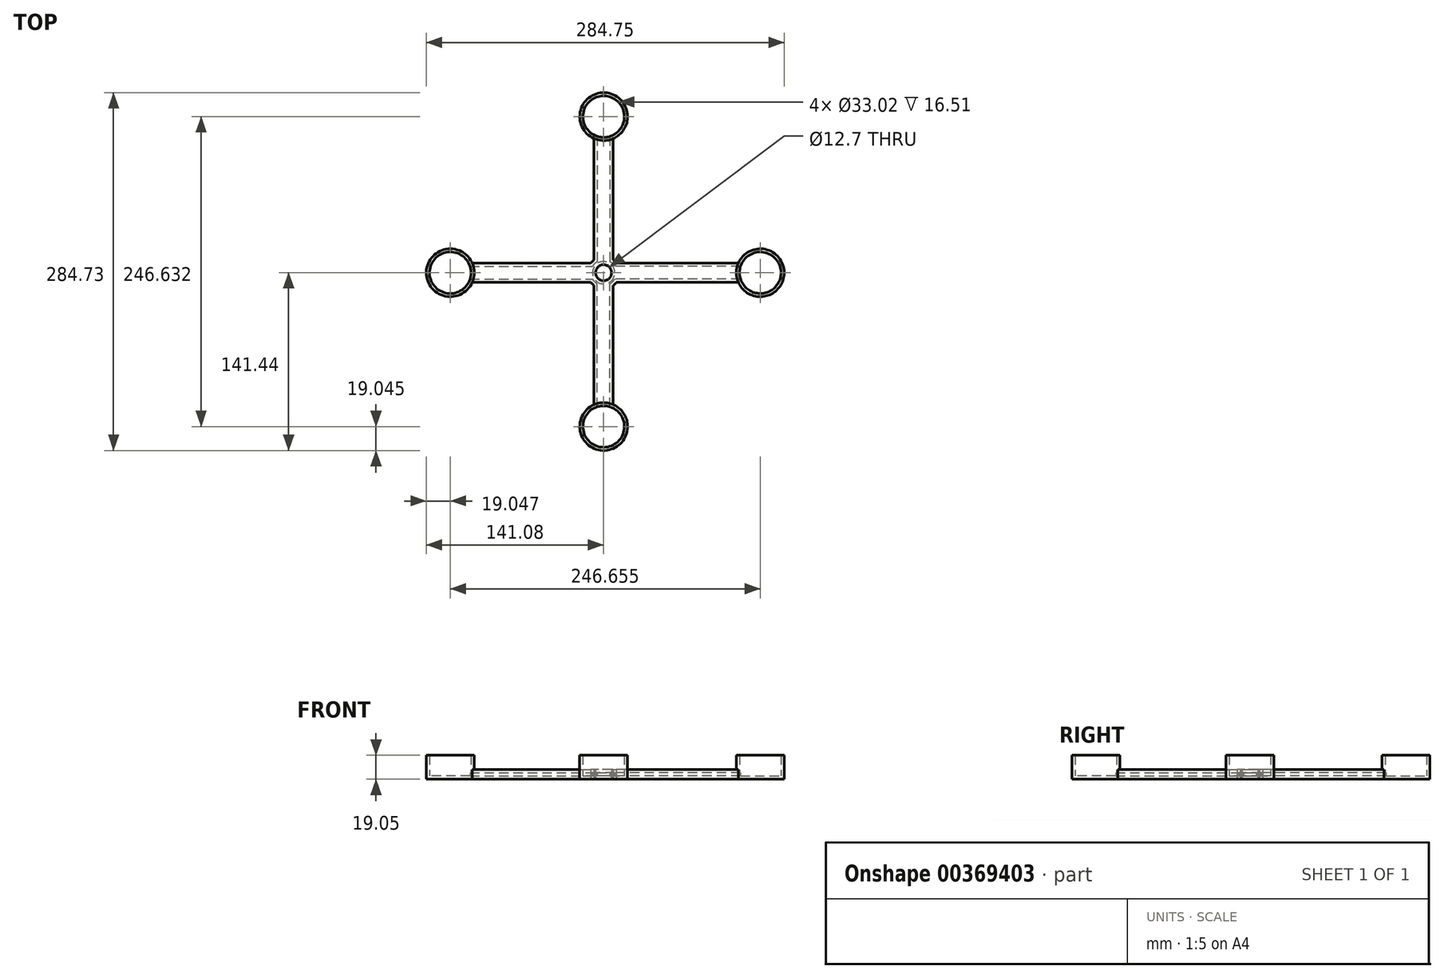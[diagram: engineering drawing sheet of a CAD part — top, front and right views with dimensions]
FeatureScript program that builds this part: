
annotation { "Feature Type Name" : "Feature", "Feature Type Description" : "" }
export const myFeature = defineFeature(function(context is Context, id is Id, definition is map)
    precondition{}
    {
        {
            var Q0;
            Q0=qCreatedBy(makeId("Top.planeOp"),FACE);
            var sketch = newSketch(context, id + "F0", { "sketchPlane" : qUnion([Q0])});
            skCircle(sketch, "E0", {"center": v(0, 0) * mm, "radius": 5 * mm});
            skCircle(sketch, "E1", {"center": v(0, 0) * mm, "radius": 3.5 * mm});
            skSolve(sketch);
        }
        {
            var Q0;
            Q0=qSketchRegion(id+"F0",true);
            extrude(context, id + "F1", {"entities" : qUnion([Q0]), "depth" : 15 * mm});
        }
        {
            var Q0;
            Q0=makeQuery(id+"F1.opExtrude","SWEPT_BODY",BODY,{"disambiguationData":[OSD([sQuery(id+"F0.wireOp",EDGE,"E0"),sQuery(id+"F0.wireOp",EDGE,"E1")])]});
            deleteBodies(context, id + "F2", {"entities" : qUnion([Q0])});
        }
        {
            var Q0;
            Q0=qCreatedBy(makeId("Front.planeOp"),FACE);
            var sketch = newSketch(context, id + "F3", { "sketchPlane" : qUnion([Q0])});
            skCircle(sketch, "E2", {"center": v(0, 0) * mm, "radius": 6.35 * mm});
            skCircle(sketch, "E3", {"center": v(0, 0) * mm, "radius": 12.7 * mm});
            skPoint(sketch, "E4.middle", {"position": v(12.7, 0) * mm});
            skLineSegment(sketch, "E5", {"start": v(-88.9, 0) * mm, "end": v(-88.9, 5.08) * mm});
            skLineSegment(sketch, "E6", {"start": v(-88.9, 0) * mm, "end": v(-88.9, -5.08) * mm});
            skLineSegment(sketch, "E7", {"start": v(88.9, 0) * mm, "end": v(88.9, -5.08) * mm});
            skLineSegment(sketch, "E8", {"start": v(88.9, 0) * mm, "end": v(88.9, 5.08) * mm});
            skLineSegment(sketch, "E9", {"start": v(0, 88.9) * mm, "end": v(5.08, 88.9) * mm});
            skLineSegment(sketch, "E10", {"start": v(0, 88.9) * mm, "end": v(-5.08, 88.9) * mm});
            skLineSegment(sketch, "E11", {"start": v(0, -88.9) * mm, "end": v(5.08, -88.9) * mm});
            skLineSegment(sketch, "E12", {"start": v(0, -88.9) * mm, "end": v(-5.08, -88.9) * mm});
            skLineSegment(sketch, "E13", {"start": v(-88.9, -5.08) * mm, "end": v(-11.64, -5.08) * mm});
            skLineSegment(sketch, "E14", {"start": v(-5.08, 88.9) * mm, "end": v(-5.08, 11.64) * mm});
            skLineSegment(sketch, "E15", {"start": v(5.08, 88.9) * mm, "end": v(5.08, 11.64) * mm});
            skLineSegment(sketch, "E16", {"start": v(88.9, 5.08) * mm, "end": v(11.64, 5.08) * mm});
            skLineSegment(sketch, "E17", {"start": v(88.9, -5.08) * mm, "end": v(11.64, -5.08) * mm});
            skLineSegment(sketch, "E18", {"start": v(5.08, -88.9) * mm, "end": v(5.08, -11.64) * mm});
            skLineSegment(sketch, "E19", {"start": v(-5.08, -88.9) * mm, "end": v(-5.08, -11.64) * mm});
            skLineSegment(sketch, "E20", {"start": v(-88.9, 5.08) * mm, "end": v(-11.64, 5.08) * mm});
            skSolve(sketch);
        }
        {
            var Q0;
            Q0=qSketchRegion(id+"F3",true);
            extrude(context, id + "F4", {"entities" : qUnion([Q0]), "depth" : 7.62 * mm});
        }
        {
            var Q0;
            Q0=makeQuery(id+"F4.opExtrude","SWEPT_BODY",BODY,{"disambiguationData":[OSD([sQuery(id+"F3.wireOp",EDGE,"E2"),sQuery(id+"F3.wireOp",EDGE,"E3"),sQuery(id+"F3.wireOp",EDGE,"E5"),sQuery(id+"F3.wireOp",EDGE,"E6"),sQuery(id+"F3.wireOp",EDGE,"E7"),sQuery(id+"F3.wireOp",EDGE,"E8"),sQuery(id+"F3.wireOp",EDGE,"E9"),sQuery(id+"F3.wireOp",EDGE,"E10"),sQuery(id+"F3.wireOp",EDGE,"E11"),sQuery(id+"F3.wireOp",EDGE,"E12"),sQuery(id+"F3.wireOp",EDGE,"E13"),sQuery(id+"F3.wireOp",EDGE,"E14"),sQuery(id+"F3.wireOp",EDGE,"E15"),sQuery(id+"F3.wireOp",EDGE,"E16"),sQuery(id+"F3.wireOp",EDGE,"E17"),sQuery(id+"F3.wireOp",EDGE,"E18"),sQuery(id+"F3.wireOp",EDGE,"E19"),sQuery(id+"F3.wireOp",EDGE,"E20")])]});
            deleteBodies(context, id + "F5", {"entities" : qUnion([Q0])});
        }
        {
            var Q0;
            Q0=qCreatedBy(makeId("Top.planeOp"),FACE);
            var sketch = newSketch(context, id + "F6", { "sketchPlane" : qUnion([Q0])});
            skCircle(sketch, "E21", {"center": v(0, 0) * mm, "radius": 6.35 * mm});
            skCircle(sketch, "E22", {"center": v(0, 0) * mm, "radius": 12.7 * mm});
            skLineSegment(sketch, "E23", {"start": v(-121.92, 0) * mm, "end": v(-121.92, -7.62) * mm});
            skLineSegment(sketch, "E24", {"start": v(-121.92, 0) * mm, "end": v(-121.92, 7.62) * mm});
            skLineSegment(sketch, "E25", {"start": v(0, 124.46) * mm, "end": v(7.62, 124.46) * mm});
            skLineSegment(sketch, "E26", {"start": v(0, 124.46) * mm, "end": v(-7.62, 124.46) * mm});
            skLineSegment(sketch, "E27", {"start": v(124.46, 0) * mm, "end": v(124.46, 7.62) * mm});
            skLineSegment(sketch, "E28", {"start": v(124.46, 0) * mm, "end": v(124.46, -7.62) * mm});
            skLineSegment(sketch, "E29", {"start": v(0, -121.92) * mm, "end": v(-7.62, -121.92) * mm});
            skLineSegment(sketch, "E30", {"start": v(0, -121.92) * mm, "end": v(7.62, -121.92) * mm});
            skLineSegment(sketch, "E31", {"start": v(-7.62, 124.46) * mm, "end": v(-7.62, 10.16) * mm});
            skLineSegment(sketch, "E32", {"start": v(7.62, 124.46) * mm, "end": v(7.62, 10.16) * mm});
            skLineSegment(sketch, "E33", {"start": v(-121.92, -7.62) * mm, "end": v(-10.16, -7.62) * mm});
            skLineSegment(sketch, "E34", {"start": v(-7.62, -121.92) * mm, "end": v(-7.62, -7.62) * mm});
            skLineSegment(sketch, "E35", {"start": v(7.62, -121.92) * mm, "end": v(7.62, -10.16) * mm});
            skLineSegment(sketch, "E36", {"start": v(124.46, 7.62) * mm, "end": v(10.16, 7.62) * mm});
            skLineSegment(sketch, "E37", {"start": v(124.46, -7.62) * mm, "end": v(10.16, -7.62) * mm});
            skLineSegment(sketch, "E38", {"start": v(-121.92, 7.62) * mm, "end": v(-7.62, 7.62) * mm});
            skSolve(sketch);
        }
        {
            var Q0;
            Q0=qSketchRegion(id+"F6",true);
            extrude(context, id + "F7", {"entities" : qUnion([Q0]), "depth" : 7.62 * mm});
        }
        {
            var Q0;
            Q0=qCreatedBy(makeId("Top.planeOp"),FACE);
            var sketch = newSketch(context, id + "F8", { "sketchPlane" : qUnion([Q0])});
            skCircle(sketch, "E39", {"center": v(-122.03, 0) * mm, "radius": 19.05 * mm});
            skCircle(sketch, "E40", {"center": v(0, 124.24) * mm, "radius": 19.05 * mm});
            skCircle(sketch, "E41", {"center": v(124.62, 0) * mm, "radius": 19.05 * mm});
            skCircle(sketch, "E42", {"center": v(0, -122.4) * mm, "radius": 19.05 * mm});
            skSolve(sketch);
        }
        {
            var Q0;
            Q0=makeQuery(id+"F8.imprint","IMPRINT",FACE,{"disambiguationData":[TD([[makeQuery(id+"F8.imprint","IMPRINT",EDGE,{"derivedFrom":sQuery(id+"F8.wireOp",EDGE,"E39")}),1.0]])]});
            var Q1;
            Q1=makeQuery(id+"F8.imprint","IMPRINT",FACE,{"disambiguationData":[TD([[makeQuery(id+"F8.imprint","IMPRINT",EDGE,{"derivedFrom":sQuery(id+"F8.wireOp",EDGE,"E40")}),1.0]])]});
            var Q2;
            Q2=makeQuery(id+"F8.imprint","IMPRINT",FACE,{"disambiguationData":[TD([[makeQuery(id+"F8.imprint","IMPRINT",EDGE,{"derivedFrom":sQuery(id+"F8.wireOp",EDGE,"E41")}),1.0]])]});
            var Q3;
            Q3=makeQuery(id+"F8.imprint","IMPRINT",FACE,{"disambiguationData":[TD([[makeQuery(id+"F8.imprint","IMPRINT",EDGE,{"derivedFrom":sQuery(id+"F8.wireOp",EDGE,"E42")}),1.0]])]});
            extrude(context, id + "F9", {"entities" : qUnion([Q0, Q1, Q2, Q3]), "operationType" : NewBodyOperationType.ADD, "depth" : 19.05 * mm});
        }
        {
            var Q0;
            Q0=makeQuery(id+"F9.opExtrude","CAP_FACE",FACE,{"disambiguationData":[OSD([sQuery(id+"F8.wireOp",EDGE,"E40")])],"isStart":false});
            var Q1;
            Q1=makeQuery(id+"F9.opExtrude","CAP_FACE",FACE,{"disambiguationData":[OSD([sQuery(id+"F8.wireOp",EDGE,"E41")])],"isStart":false});
            var Q2;
            Q2=makeQuery(id+"F9.opExtrude","CAP_FACE",FACE,{"disambiguationData":[OSD([sQuery(id+"F8.wireOp",EDGE,"E42")])],"isStart":false});
            var Q3;
            Q3=makeQuery(id+"F9.opExtrude","CAP_FACE",FACE,{"disambiguationData":[OSD([sQuery(id+"F8.wireOp",EDGE,"E39")])],"isStart":false});
            shell(context, id + "F10", {"entities" : qUnion([Q0, Q1, Q2, Q3]), "thickness" : 2.54 * mm});
        }
    });
